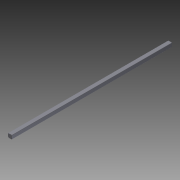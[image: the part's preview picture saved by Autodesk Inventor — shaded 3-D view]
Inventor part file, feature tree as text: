
AUTODESK INVENTOR PART (.ipt)
format: ipt  version: 2014 SP1 (Build 180222100, 222)  size: 163,328 bytes
history: native  units: in
note: dims shown in document units (in); Inventor stores cm internally (conversion verified against a paired STEP export)
features: projected_geometry x8, other x1, imported_body x1, extrude x1, sketch x1
ambient origin geometry x8: Origin, YZ Plane, XZ Plane, XY Plane, X Axis, Y Axis, Z Axis, Center Point
bodies: Body1 (feature_tree)
feature tree (12):
  parser-record x1  (decoder bookkeeping rows leaked as tree rows — omitted from the tree; the rows remain in map.json)
  imported_body  "Base1"
  extrude  "Extrusion1"  [1 undecoded]
  sketch  "Sketch1"  dims[d0=5.2in d1=0.0in]
  projected_geometry  "Projected Loop1"
  projected_geometry  "Projected Loop2"
  projected_geometry  "Projected Loop3"
  projected_geometry  "Projected Loop4"
  projected_geometry  "Projected Loop5"
  projected_geometry  "Projected Loop6"
  projected_geometry  "Projected Loop7"
  projected_geometry  "Projected Loop8"
note: 1 required parameter value undecoded (feature->parameter linkage not recoverable at this tier; creation-order binding heuristic only, values carry confidence <= 0.55)
